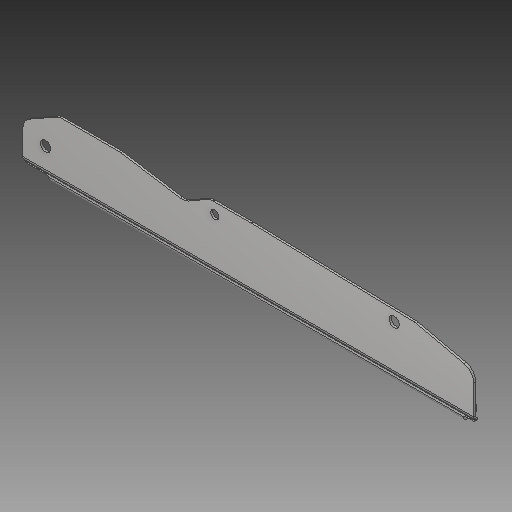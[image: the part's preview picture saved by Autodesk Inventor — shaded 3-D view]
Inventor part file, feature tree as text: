
AUTODESK INVENTOR PART (.ipt)
format: ipt  version: 2019 (Build 230136000, 136)  size: 260,608 bytes
history: native  units: mm
features: sketch x5, sheet_metal_op x4, projected_geometry x4, fillet x3, extrude x2, hole x2, other x2
ambient origin geometry x8: Origin, YZ Plane, XZ Plane, XY Plane, X Axis, Y Axis, Z Axis, Center Point
bodies: Solid1 (feature_tree)
feature tree (22):
  sheet_metal_op  "Face1"
  sheet_metal_op  "Contour Flange1"
  extrude  "Extrusion1"  Depth=2.0mm
  extrude  "Extrusion2"  Depth=2.0mm
  fillet  "Fillet1"  Radius=2.25mm
  fillet  "Fillet2"  Radius=2.0mm
  fillet  "Fillet3"  Radius=1.0mm
  sketch  "Sketch5"  dims[d35=2.0mm d36=2.0mm d37=8.0mm d38=2.0mm d39=2.0mm d41=5.6mm d42=23.0mm d43=0.0mm d44=12.0mm d45=0.0mm d46=12.0mm d47=4.0mm d48=2.0mm d65=22.0mm d68=186.0mm d70=360.0mm d72=10.0mm d73=6.0mm d74=4.0mm d75=2.0mm d76=90.0deg d77=2.0mm d78=20.594885mm d79=8.15mm d80=6.0mm d81=4.0mm d82=2.0mm d83=90.0deg d84=2.0mm d85=20.594885mm d86=52.0mm d87=30.5mm d88=55.0mm]
  hole  "Hole1"  [1 undecoded]
  hole  "Hole2"  [1 undecoded]
  sketch  "Sketch1"  dims[d0=50.842275mm d1=31.0mm d2=35.0mm d3=59.0mm d4=1.570796mm d5=4.0mm d6=40.0mm d7=38.0mm d8=57.0mm d9=437.0mm d10=63.0mm d11=24.0mm d12=2.0mm]
  other  "Plate1"
  sketch  "Sketch2"  dims[d13=50.9mm]
  other  "Plate2"
  sheet_metal_op  "Bend1"
  sheet_metal_op  "Corner1"
  sketch  "Sketch3"  dims[d17=9.0mm d23=4.0mm d25=2.0mm d26=2.0mm d27=2.0mm d29=0.666667mm d30=2.25mm d31=2.0mm d32=1.0mm]
  sketch  "Sketch4"  dims[d33=4.0mm d34=2.0mm]
  projected_geometry  "Projected Loop2"
  projected_geometry  "Projected Loop3"
  projected_geometry  "Projected Loop4"
  projected_geometry  "Projected Loop5"
note: 2 required parameter values undecoded (feature->parameter linkage not recoverable at this tier; creation-order binding heuristic only, values carry confidence <= 0.55)
